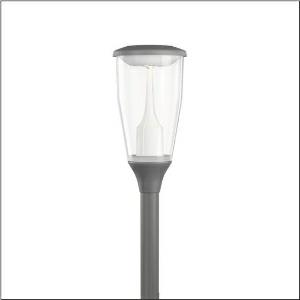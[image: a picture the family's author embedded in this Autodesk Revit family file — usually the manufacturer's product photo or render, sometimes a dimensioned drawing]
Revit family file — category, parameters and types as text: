
# Revit family: dl_11_iq___p1_0a_5xa5565nf14hp00022_fef3
name_source: partatom
category: Lighting Fixtures
units: mm (PartAtom-declared; Revit-internal decimal feet)

## family parameters
Cut with Voids When Loaded = No
Host = Face
Light Source = No
Part Type = Normal
Room Calculation Point = No
Round Connector Dimension = Use Diameter
Shared = No

## types (1)
- --- (1 x LED, 4280 lm, 33.6 W, 2700K)
    Apparent Load = 34 VA
    CIE Flux Codes = 33 63 91 94 100
    Color Rendering = 70
    Color Temperature = 2700K
    Default Elevation = 1800 mm
    Description = DL 11 iQ, mast luminaire, Module 540 iQ-SR, primary light control with 3 zone facetted reflector, of plastic, silver coated, highly specular, structured, primary optical cover: cover, of PMMA, transparent, light distribution: P1.0a, light emission: direct distribution, primary light characteristic: asymmetric, installation type: post-top, LED, High Power LED, light colour: 727, colour temperature: 2700K, control gear: iQ Street-Remote, control: Street-Remote, Auto-Match, Temp-Guard, Lumen-Switch, Night-Set, Smart-Wire, Light-Fading, Desk-Remote (wireless, voltage-free reading and setting of iQ features in the workshop via application-optimized NFC function/RFID function), optimised constant luminous flux control (CLO 2.0), mains connection: 220..240V, AC, 50/60Hz, connection cable pre-assembled, cable length: 5,5m, start of lifetime: 34W, end of service life: 36W, luminaire housing, upper part, of diecast aluminium, coated, Siteco® metallic grey (DB 702S), spigot size: 60mm (post-top), mounting height: 3..5m, post-top mast mounting element, of diecast aluminium, coated, Siteco® metallic grey (DB 702S), Module 540 iQ-SR, traffic white (RAL 9016), equipment: Power, protection rating (complete): IP66, insulation class (complete): insulation class II (safety insulation), certification: CE, ENEC, ENEC+, VDE, impact resistance: IK07, packaging unit: 1 piece

Light Distribution: P1.0a
    Height = 665 mm
    Lamp = 1 x LED
    Lamp Light Flux = 4280 lm
    Lamp Power = 33.6 W
    Lamp count = 1
    Length = 334 mm
    Luminous efficacy = 127 lm/W
    Manufacturer = Siteco
    ModVariant = No
    Model = 5XA5565NF14HP00022
    Number of Poles = 1
    OnlyDefault = Yes
    Power Factor = 1
    Product Name = DL 11 iQ | P1.0a
    Product group = mast luminaire | pylon top
    ProductGroupID = 6100
    Protection Class = Protection class II
    Protection Degree = IP 66
    RLX_Detail_Level = 1
    RLX_Emergency_Light_Flux = 0 lm
    RLX_Emergency_Type = 0
    RLX_Emergency_Type_DB = No
    RlxData = <blob elided: 105629 chars, md5=068c8db9>
    Socket = socket
    Standby Power = 0 W
    System Light Flux = 4280 lm
    System Power = 34 W
    Type Comments = factory setting: luminous flux: 100 % | dim-lin: 254 | 695 mA
    Type Image = l_1258354.jpg
    URL = http://relux.com
    VarID = @adj_053329
    Voltage = 0 V
    Weight = 0.00 kg
    Width = 0 mm  [stored 0 ft]

note: [stored X ft] marks values corroborated as IEEE doubles in the binary element streams (Revit-internal decimal feet)

## geometry (parser evidence)
native form markers: Blend x4, Sweep x10
no freeform markers — native parametric forms only
